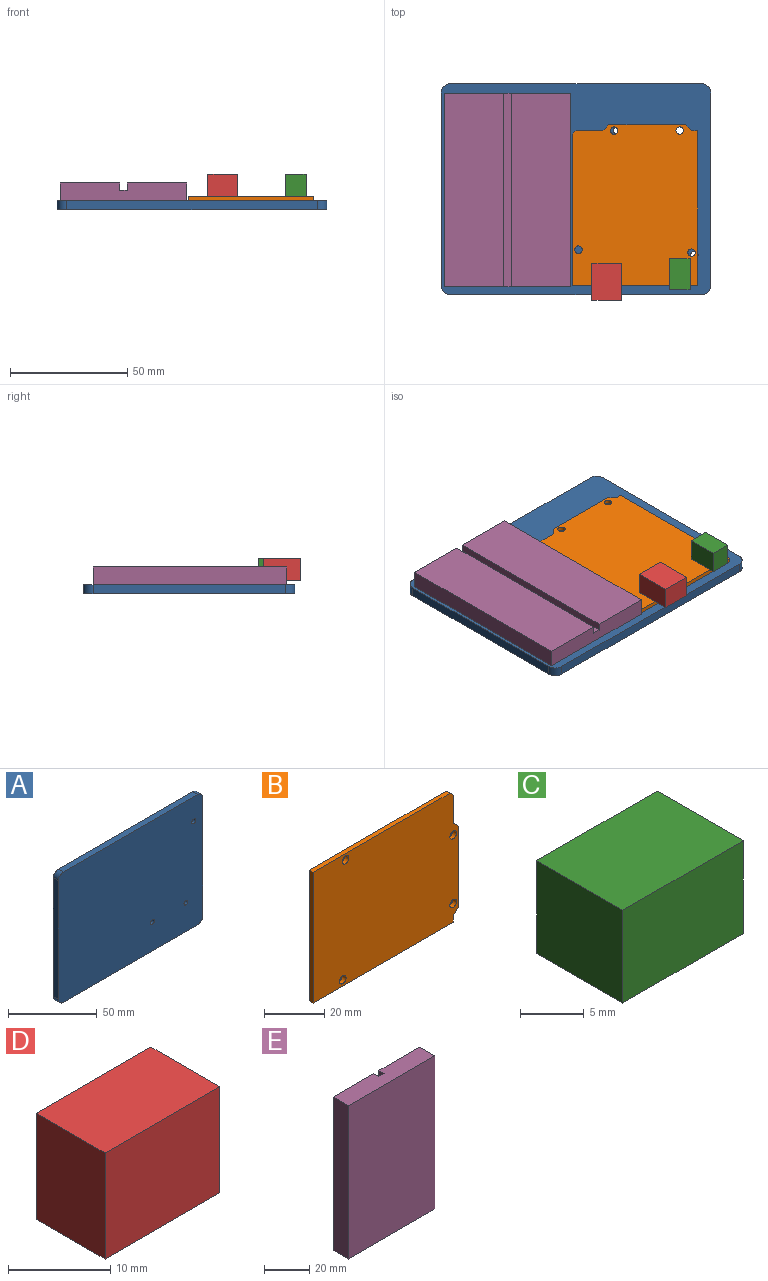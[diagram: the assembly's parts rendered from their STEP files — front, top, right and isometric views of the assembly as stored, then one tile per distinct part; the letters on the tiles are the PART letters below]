
ASSEMBLY  parts=5 mates=4
PART A: 18 faces, bbox 115x4x90 mm
  f0: plane 115x90mm, normal (0,1,0), area 5856.9mm2, adj f1,f2,f3,f4,f5,f6,f7,f8
  f1: plane 107x4mm, normal (0,0,-1), area 428mm2, adj f0,f2,f8,f9
  f2: cylinder r=4mm len=4mm, axis (0,1,0), area 25.1mm2, adj f0,f1,f3,f9
  f3: plane 82x4mm, normal (1,0,0), area 328mm2, adj f0,f2,f4,f9
  f4: cylinder r=4mm len=4mm, axis (0,1,0), area 25.1mm2, adj f0,f3,f5,f9
  f5: plane 107x4mm, normal (0,0,1), area 428mm2, adj f0,f4,f6,f9
  f6: cylinder r=4mm len=4mm, axis (0,1,0), area 25.1mm2, adj f0,f5,f7,f9
  f7: plane 82x4mm, normal (-1,0,0), area 328mm2, adj f0,f6,f8,f9
  f8: cylinder r=4mm len=4mm, axis (0,1,0), area 25.1mm2, adj f0,f1,f7,f9
  f9: plane 115x90mm, normal (0,-1,0), area 10312.5mm2, adj f1,f2,f3,f4,f5,f6,f7,f8
  f10: cylinder r=1.59mm len=4mm, axis (0,-1,0), area 39.9mm2, adj f0,f9
  f11: cylinder r=1.59mm len=4mm, axis (0,-1,0), area 39.9mm2, adj f0,f9
  f12: cylinder r=1.59mm len=4mm, axis (0,-1,0), area 39.9mm2, adj f0,f9
  f13: plane 53.98x2.03mm, normal (0,0,-1), area 109.7mm2, adj f0,f14,f16,f17
  f14: plane 82.55x2.03mm, normal (-1,0,0), area 167.7mm2, adj f0,f13,f15,f17
  f15: plane 53.98x2.03mm, normal (0,0,1), area 109.7mm2, adj f0,f14,f16,f17
  f16: plane 82.55x2.03mm, normal (1,0,0), area 167.7mm2, adj f0,f13,f15,f17
  f17: plane 82.55x53.98mm, normal (0,1,0), area 4455.6mm2, adj f13,f14,f15,f16
PART B: 15 faces, bbox 68.6x1.8x53.3 mm
  f0: plane 53.34x1.78mm, normal (-1,0,0), area 94.8mm2, adj f1,f12,f13,f14
  f1: plane 66.04x1.78mm, normal (0,0,-1), area 117.4mm2, adj f0,f2,f13,f14
  f2: plane 2.54x1.78mm, normal (1,0,0), area 4.5mm2, adj f1,f3,f13,f14
  f3: plane 2.54x2.54mm, normal (0.71,0,-0.71), area 6.4mm2, adj f2,f4,f13,f14
  f4: plane 32.77x1.78mm, normal (1,0,0), area 58.3mm2, adj f3,f5,f13,f14
  f5: plane 2.54x2.54mm, normal (0.71,0,0.71), area 6.4mm2, adj f4,f6,f13,f14
  f6: plane 11.43x1.78mm, normal (1,0,0), area 20.3mm2, adj f5,f7,f13,f14
  f7: plane 1.78x1.52mm, normal (0.71,0,0.71), area 3.8mm2, adj f6,f12,f13,f14
  f8: cylinder r=1.59mm len=3.18mm, axis (0,1,0), area 17.7mm2, adj f13,f14
  f9: cylinder r=1.59mm len=3.18mm, axis (0,1,0), area 17.7mm2, adj f13,f14
  f10: cylinder r=1.59mm len=3.18mm, axis (0,1,0), area 17.7mm2, adj f13,f14
  f11: cylinder r=1.59mm len=3.18mm, axis (0,1,0), area 17.7mm2, adj f13,f14
  f12: plane 64.52x1.78mm, normal (0,0,1), area 114.7mm2, adj f0,f7,f13,f14
  f13: plane 68.58x53.34mm, normal (0,-1,0), area 3579.4mm2, adj f0,f1,f2,f3,f4,f5,f6,f7
  f14: plane 68.58x53.34mm, normal (0,1,0), area 3579.4mm2, adj f0,f1,f2,f3,f4,f5,f6,f7
PART C: 6 faces, bbox 13.3x9.5x8.9 mm
  f0: plane 9.53x8.89mm, normal (1,0,0), area 84.7mm2, adj f1,f3,f4,f5
  f1: plane 13.34x9.53mm, normal (0,0,1), area 127mm2, adj f0,f2,f4,f5
  f2: plane 9.53x8.89mm, normal (-1,0,0), area 84.7mm2, adj f1,f3,f4,f5
  f3: plane 13.34x9.53mm, normal (0,0,-1), area 127mm2, adj f0,f2,f4,f5
  f4: plane 13.34x8.89mm, normal (0,-1,0), area 118.5mm2, adj f0,f1,f2,f3
  f5: plane 13.34x8.89mm, normal (0,1,0), area 118.5mm2, adj f0,f1,f2,f3
PART D: 6 faces, bbox 15.9x9.5x12.7 mm
  f0: plane 15.88x9.53mm, normal (0,0,-1), area 151.2mm2, adj f1,f3,f4,f5
  f1: plane 12.7x9.53mm, normal (1,0,0), area 121mm2, adj f0,f2,f4,f5
  f2: plane 15.88x9.53mm, normal (0,0,1), area 151.2mm2, adj f1,f3,f4,f5
  f3: plane 12.7x9.53mm, normal (-1,0,0), area 121mm2, adj f0,f2,f4,f5
  f4: plane 15.88x12.7mm, normal (0,-1,0), area 201.6mm2, adj f0,f1,f2,f3
  f5: plane 15.88x12.7mm, normal (0,1,0), area 201.6mm2, adj f0,f1,f2,f3
PART E: 10 faces, bbox 54x9.5x82.6 mm
  f0: plane 82.55x25.4mm, normal (0,1,0), area 2096.8mm2, adj f1,f2,f4,f7
  f1: plane 53.98x9.53mm, normal (0,0,1), area 504mm2, adj f0,f2,f3,f5,f6,f7,f8,f9
  f2: plane 82.55x9.53mm, normal (1,0,0), area 786.3mm2, adj f0,f1,f4,f6
  f3: plane 82.55x9.53mm, normal (-1,0,0), area 786.3mm2, adj f1,f4,f5,f6
  f4: plane 53.98x9.53mm, normal (0,0,-1), area 504mm2, adj f0,f2,f3,f5,f6,f7,f8,f9
  f5: plane 82.55x25.4mm, normal (0,1,0), area 2096.8mm2, adj f1,f3,f4,f8
  f6: plane 82.55x53.98mm, normal (0,-1,0), area 4455.6mm2, adj f1,f2,f3,f4
  f7: plane 82.55x3.18mm, normal (-1,0,0), area 262.1mm2, adj f0,f1,f4,f9
  f8: plane 82.55x3.18mm, normal (1,0,0), area 262.1mm2, adj f1,f4,f5,f9
  f9: plane 82.55x3.18mm, normal (0,1,0), area 262.1mm2, adj f1,f4,f7,f8
PLACE A rot(axis=(1,0,0),90deg) t=(29.81,-54.06,52.72)mm
PLACE B rot(axis=(-0.58,-0.58,0.58),120deg) t=(74.94,-52.17,52.72)mm
PLACE C rot(axis=(-0.58,-0.58,0.58),120deg) t=(74.94,-52.17,52.72)mm
PLACE D rot(axis=(-0.58,-0.58,0.58),120deg) t=(74.94,-52.17,52.72)mm
PLACE E rot(axis=(1,0,0),90deg) t=(0.57,-54.34,50.69)mm
MATE fastened E.f6 <-> A.f17  axis (0,0,-1) through (-26.42,-95.61,50.69)mm
MATE fastened A.f10 <-> B.f9  axis (0,0,1) through (74.03,-29.06,52.72)mm
MATE fastened C.f5 <-> B.f13  axis (0,0,-1) through (78.48,-97.01,54.5)mm
MATE fastened D.f5 <-> B.f13  axis (0,0,-1) through (36.57,-101.45,54.5)mm
